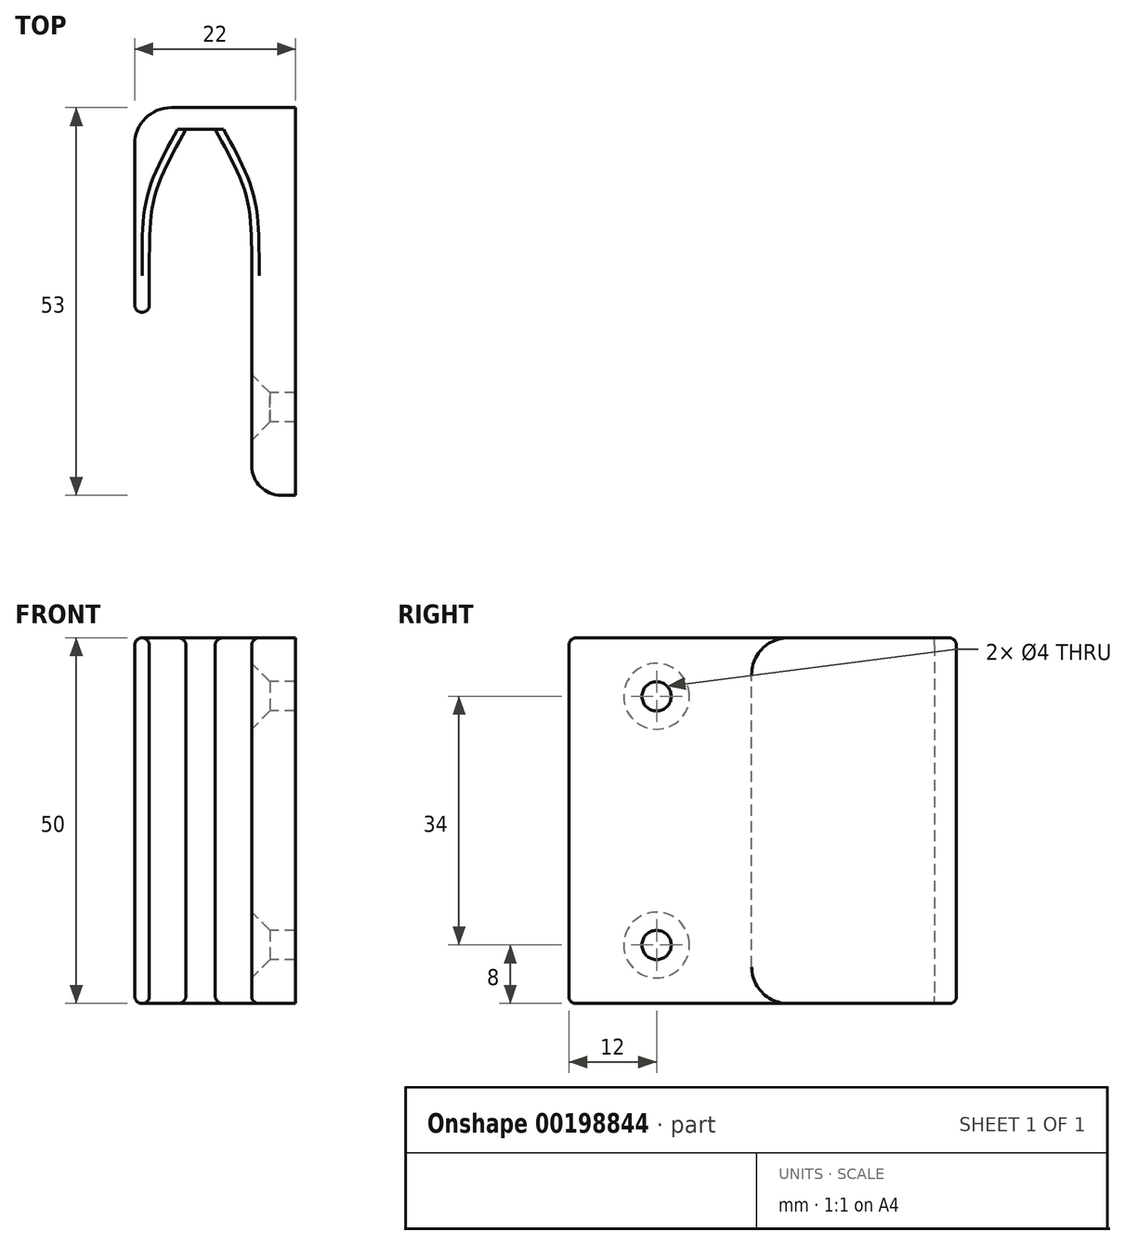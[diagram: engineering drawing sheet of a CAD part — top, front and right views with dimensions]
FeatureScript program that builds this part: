
annotation { "Feature Type Name" : "Feature", "Feature Type Description" : "" }
export const myFeature = defineFeature(function(context is Context, id is Id, definition is map)
    precondition{}
    {
        {
            var Q0;
            Q0=qCreatedBy(makeId("Top.planeOp"),FACE);
            var sketch = newSketch(context, id + "F0", { "sketchPlane" : qUnion([Q0])});
            skLineSegment(sketch, "E0.bottom", {"start": v(11, -25) * mm, "end": v(-11, -25) * mm});
            skLineSegment(sketch, "E0.top", {"start": v(11, 25) * mm, "end": v(-11, 25) * mm});
            skLineSegment(sketch, "E0.left", {"start": v(11, -25) * mm, "end": v(11, 25) * mm});
            skLineSegment(sketch, "E0.right", {"start": v(-11, -25) * mm, "end": v(-11, 25) * mm});
            skPoint(sketch, "E0.middle", {"position": v(0, 0) * mm});
            skLineSegment(sketch, "E1", {"start": v(-11, 0) * mm, "end": v(-9, 0) * mm});
            skPoint(sketch, "E1.endSnap0", {"position": v(-11, 0) * mm});
            skLineSegment(sketch, "E2", {"start": v(-9, 0) * mm, "end": v(-9, 5) * mm});
            skFitSpline(sketch, "E3", {"points": [v(-9, 5) * mm, v(-4, 25) * mm], "startDerivative": vector(0, 30) * mm, "endDerivative": vector(15, 26.7) * mm});
            skLineSegment(sketch, "E4", {"start": v(5, -25) * mm, "end": v(5, 25) * mm});
            skLineSegment(sketch, "E5", {"start": v(-2, 25) * mm, "end": v(-2, 0) * mm});
            skFitSpline(sketch, "E6.MirrorCS", {"points": [v(5, 5) * mm, v(0, 25) * mm], "startDerivative": vector(0, 30) * mm, "endDerivative": vector(-15, 26.7) * mm});
            skLineSegment(sketch, "E7.bottom", {"start": v(-11, 25) * mm, "end": v(11, 25) * mm});
            skLineSegment(sketch, "E7.top", {"start": v(-11, 28) * mm, "end": v(11, 28) * mm});
            skLineSegment(sketch, "E7.left", {"start": v(-11, 25) * mm, "end": v(-11, 28) * mm});
            skLineSegment(sketch, "E7.right", {"start": v(11, 25) * mm, "end": v(11, 28) * mm});
            skSolve(sketch);
        }
        {
            var Q0;
            {var subQ1=sQuery(id+"F0.wireOp",EDGE,"E1");Q0=makeQuery(id+"F0.imprint","IMPRINT",FACE,{"disambiguationData":[TD([[makeQuery(id+"F0.imprint","IMPRINT",EDGE,{"derivedFrom":subQ1}),1.0]])]});}
            var Q1;
            Q1=makeQuery(id+"F0.imprint","IMPRINT",FACE,{"disambiguationData":[TD([[makeQuery(id+"F0.imprint","IMPRINT",EDGE,{"derivedFrom":sQuery(id+"F0.wireOp",EDGE,"E7.top")}),-1.0]])]});
            var Q2;
            {var subQ3=sQuery(id+"F0.wireOp",EDGE,"E6.MirrorCS");Q2=makeQuery(id+"F0.imprint","IMPRINT",FACE,{"disambiguationData":[TD([[makeQuery(id+"F0.imprint","IMPRINT",EDGE,{"derivedFrom":subQ3}),-1.0]])]});}
            var Q3;
            {var subQ4=sQuery(id+"F0.wireOp",EDGE,"E0.left");Q3=makeQuery(id+"F0.imprint","IMPRINT",FACE,{"disambiguationData":[TD([[makeQuery(id+"F0.imprint","IMPRINT",EDGE,{"derivedFrom":subQ4}),1.0]])]});}
            extrude(context, id + "F1", {"entities" : qUnion([Q0, Q1, Q2, Q3]), "depth" : 50 * mm});
        }
        {
            var Q0;
            Q0=makeQuery(id+"F1.opExtrude","SWEPT_EDGE",EDGE,{"disambiguationData":[OSD([sQuery(id+"F0.wireOp",EDGE,"E0.bottom"),sQuery(id+"F0.wireOp",EDGE,"E4")])]});
            fillet(context, id + "F2", {"entities" : qUnion([Q0]), "radius" : 4 * mm, "tangentPropagation" : true, "allowEdgeOverflow" : false});
        }
        {
            var Q0;
            Q0=makeQuery(id+"F1.opExtrude","SWEPT_EDGE",EDGE,{"disambiguationData":[OSD([sQuery(id+"F0.wireOp",EDGE,"E7.top"),sQuery(id+"F0.wireOp",EDGE,"E7.left")])]});
            fillet(context, id + "F3", {"entities" : qUnion([Q0]), "radius" : 5 * mm, "tangentPropagation" : true, "allowEdgeOverflow" : false});
        }
        {
            var Q0;
            Q0=makeQuery(id+"F1.opExtrude","SWEPT_FACE",FACE,{"disambiguationData":[OSD([sQuery(id+"F0.wireOp",EDGE,"E4")])]});
            var sketch = newSketch(context, id + "F4", { "sketchPlane" : qUnion([Q0])});
            skPoint(sketch, "E8", {"position": v(13, 42) * mm});
            skPoint(sketch, "E9", {"position": v(13, 8) * mm});
            skSolve(sketch);
        }
        {
            var Q0;
            Q0=sQuery(id+"F4.wireOp",VERTEX,"E8");
            var Q1;
            Q1=sQuery(id+"F4.wireOp",VERTEX,"E9");
            var Q2;
            Q2=makeQuery(id+"F1.opExtrude","SWEPT_BODY",BODY,{"disambiguationData":[OSD([sQuery(id+"F0.wireOp",EDGE,"E0.bottom"),sQuery(id+"F0.wireOp",EDGE,"E0.left"),sQuery(id+"F0.wireOp",EDGE,"E0.right"),sQuery(id+"F0.wireOp",EDGE,"E1"),sQuery(id+"F0.wireOp",EDGE,"E2"),sQuery(id+"F0.wireOp",EDGE,"E3"),sQuery(id+"F0.wireOp",EDGE,"E4"),sQuery(id+"F0.wireOp",EDGE,"E6.MirrorCS"),sQuery(id+"F0.wireOp",EDGE,"E7.bottom"),sQuery(id+"F0.wireOp",EDGE,"E7.top"),sQuery(id+"F0.wireOp",EDGE,"E7.left"),sQuery(id+"F0.wireOp",EDGE,"E7.right")])]});
            hole(context, id + "F5", {"style" : HoleStyle.C_SINK, "endStyle" : HoleEndStyle.BLIND, "holeDiameter" : 4 * mm, "cSinkDiameter" : 9 * mm, "cSinkAngle" : 90 * degree, "holeDepth" : 25 * mm, "startFromSketch" : true, "locations" : qUnion([Q0, Q1]), "scope" : qUnion([Q2])});
        }
        {
            var Q0;
            Q0=makeQuery(id+"F1.opExtrude","CAP_EDGE",EDGE,{"disambiguationData":[OSD([sQuery(id+"F0.wireOp",EDGE,"E1")])],"isStart":false});
            var Q1;
            Q1=makeQuery(id+"F1.opExtrude","CAP_EDGE",EDGE,{"disambiguationData":[OSD([sQuery(id+"F0.wireOp",EDGE,"E1")])],"isStart":true});
            fillet(context, id + "F6", {"entities" : qUnion([Q0, Q1]), "radius" : 5 * mm, "tangentPropagation" : true, "allowEdgeOverflow" : false});
        }
        {
            var Q0;
            Q0=makeQuery(id+"F1.opExtrude","SWEPT_EDGE",EDGE,{"disambiguationData":[OSD([sQuery(id+"F0.wireOp",EDGE,"E0.right"),sQuery(id+"F0.wireOp",EDGE,"E1")])]});
            var Q1;
            Q1=makeQuery(id+"F1.opExtrude","SWEPT_EDGE",EDGE,{"disambiguationData":[OSD([sQuery(id+"F0.wireOp",EDGE,"E1"),sQuery(id+"F0.wireOp",EDGE,"E2")])]});
            var Q2;
            Q2=makeQuery(id+"F1.opExtrude","CAP_EDGE",EDGE,{"disambiguationData":[OSD([sQuery(id+"F0.wireOp",EDGE,"E7.bottom")])],"isStart":true});
            var Q3;
            Q3=makeQuery(id+"F1.opExtrude","CAP_EDGE",EDGE,{"disambiguationData":[OSD([sQuery(id+"F0.wireOp",EDGE,"E6.MirrorCS")])],"isStart":true});
            var Q4;
            Q4=makeQuery(id+"F1.opExtrude","CAP_EDGE",EDGE,{"disambiguationData":[OSD([sQuery(id+"F0.wireOp",EDGE,"E4")])],"isStart":false});
            var Q5;
            Q5=makeQuery(id+"F1.opExtrude","CAP_EDGE",EDGE,{"disambiguationData":[OSD([sQuery(id+"F0.wireOp",EDGE,"E7.bottom")])],"isStart":false});
            fillet(context, id + "F7", {"entities" : qUnion([Q0, Q1, Q2, Q3, Q4, Q5]), "radius" : 1 * mm, "tangentPropagation" : true, "allowEdgeOverflow" : false});
        }
    });
